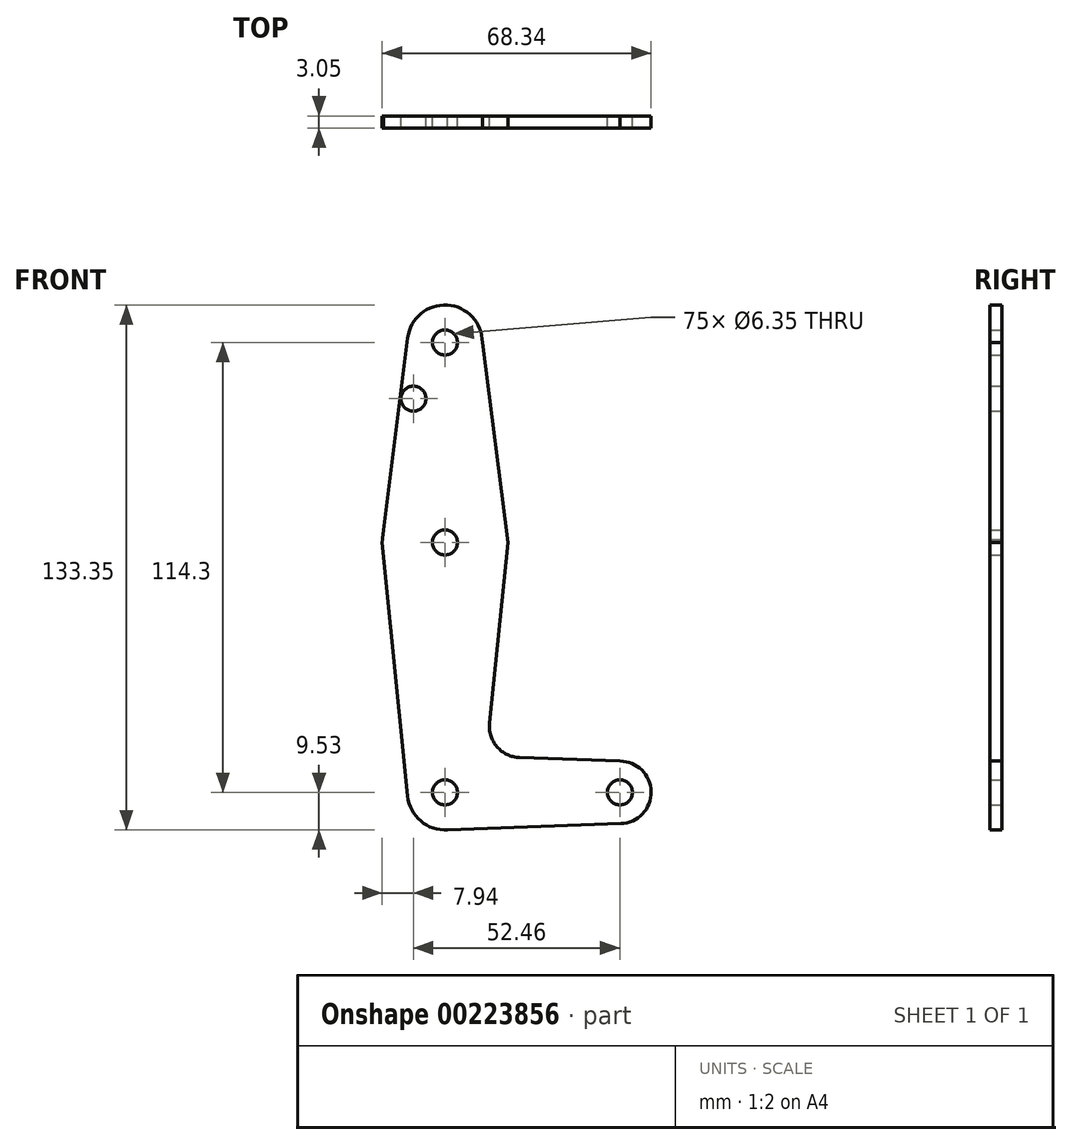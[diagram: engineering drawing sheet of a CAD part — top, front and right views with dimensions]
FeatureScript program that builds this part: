
annotation { "Feature Type Name" : "Feature", "Feature Type Description" : "" }
export const myFeature = defineFeature(function(context is Context, id is Id, definition is map)
    precondition{}
    {
        {
            var Q0;
            Q0=qCreatedBy(makeId("Front.planeOp"),FACE);
            var sketch = newSketch(context, id + "F0", { "sketchPlane" : qUnion([Q0])});
            skCircle(sketch, "E0", {"center": v(0, 50.8) * mm, "radius": 9.53 * mm});
            skCircle(sketch, "E1", {"center": v(0, 0) * mm, "radius": 15.88 * mm});
            skCircle(sketch, "E2", {"center": v(0, -63.5) * mm, "radius": 9.53 * mm});
            skCircle(sketch, "E3", {"center": v(44.45, -63.5) * mm, "radius": 7.94 * mm});
            skLineSegment(sketch, "E4", {"start": v(0, 50.8) * mm, "end": v(0, 0) * mm});
            skLineSegment(sketch, "E5", {"start": v(0, 0) * mm, "end": v(0, -63.5) * mm});
            skLineSegment(sketch, "E6", {"start": v(0, -63.5) * mm, "end": v(44.45, -63.5) * mm});
            skLineSegment(sketch, "E7", {"start": v(9.53, 50.8) * mm, "end": v(16, 0) * mm});
            skLineSegment(sketch, "E8", {"start": v(16, 0) * mm, "end": v(11.32, -45.9) * mm});
            skLineSegment(sketch, "E9", {"start": v(18.95, -54.65) * mm, "end": v(44.45, -55.56) * mm});
            skLineSegment(sketch, "E10", {"start": v(0, -73.03) * mm, "end": v(44.73, -71.43) * mm});
            skLineSegment(sketch, "E11", {"start": v(-9.45, 51.98) * mm, "end": v(-15.95, 0) * mm});
            skLineSegment(sketch, "E12", {"start": v(-15.95, 0) * mm, "end": v(-9.48, -64.45) * mm});
            skCircle(sketch, "E13", {"center": v(0, 50.8) * mm, "radius": 3.18 * mm});
            skCircle(sketch, "E14", {"center": v(0, 0) * mm, "radius": 3.18 * mm});
            skCircle(sketch, "E15", {"center": v(0, -63.5) * mm, "radius": 3.18 * mm});
            skCircle(sketch, "E16", {"center": v(44.45, -63.5) * mm, "radius": 3.18 * mm});
            skCircle(sketch, "E17", {"center": v(-8.01, 36.53) * mm, "radius": 3.18 * mm});
            skArc(sketch, "E18.filletArc", {"start": v(11.32, -45.9) * mm, "mid": v(13.24, -51.93) * mm, "end": v(18.95, -54.65) * mm});
            skSolve(sketch);
        }
        {
            var Q0;
            Q0 = qSketchRegion(id + "F0", true);
            var Q1;
            {var subQ0=sQuery(id+"F0.wireOp",EDGE,"E5");var subQ1=sQuery(id+"F0.wireOp",EDGE,"E2");var subQ2=makeQuery(id+"F0.imprint","INTERSECT",VERTEX,{"derivedFrom":[subQ1,subQ0]});Q1=makeQuery(id+"F0.imprint","IMPRINT",FACE,{"disambiguationData":[TD([[makeQuery(id+"F0.imprint","IMPRINT",EDGE,{"disambiguationData":[TD([[subQ2,1.0]])],"derivedFrom":subQ1}),1.0]])]});}
            extrude(context, id + "F1", {"entities" : qUnion([Q0, Q1]), "depth" : 3.05 * mm});
        }
    });
